# Revit family: Malvestio_Delta 4_CriticalCare___
name_source: partatom
category: Furniture
revit_build: Autodesk Revit 2018 (Build: 20190510_1515(x64)
units: mm (PartAtom-declared; Revit-internal decimal feet)

## family parameters
Always vertical = Yes
Cut with Voids When Loaded = No
OmniClass Number = 23.40.20.17.14.11
OmniClass Title = Beds
Room Calculation Point = No
Shared = No
Work Plane-Based = No

## types (2) — shared parameters
Bed_H Max = 800 mm
Bed_H Min = 390 mm
Bed_Inc Max = 16.00°
Bed_Inc Min = -16.00°
Bed_Lat Max = 15.00°
Bed_Lat Min = -15.00°
Blanket and Surpevisor Holder = Yes
DIM_Depth = 1000 mm  [stored 3.28084 ft]
DIM_Height = 1300 mm  [stored 4.26509 ft]
DIM_Mattress_Thick = 150 mm  [stored 0.492126 ft]
DIM_Width = 2200 mm
Ele_FL Amps = 0 A
Ele_Frequency = 50 Hz
Ele_Power = 0 W
Ele_Volts = 240 V
Frame_Base offset = 190 mm  [stored 0.62336 ft]
Frame_Boom = 540 mm
Frame_Top width = 255 mm  [stored 0.836614 ft]
Keynote = 0
Manufacturer = Malvestio Spa
Mat_Bump = Rubber Gray
Mat_CallUp = RAL 7032
Mat_Case = RAL 9010
Mat_Panel = RAL 9010
Mat_Panel_Logo = AB 425_Lilla Erica
Mat_Weel_Tyre = Rubber Black
Product Disclaimer = Malvestio Spa declines any responsibility for
the modifications of the type parameters.
The company is not responsible for the
objects/drawings and the correct
production/installation.
The company reserves the right to make technical
improvements or modifications of any type without
prior notice to the customer.
All rights reserved.
Product Series = Delta 4
Product URL = https://www.malvestio.com
URL = https://www.malvestio.com
Weighing System = Yes
Weight = 240.00 kg

## per-type parameters (varying)
| type | Electric Controls Side-Rails | Model | Product Code | Product Model |
| 3730B_AB 425_Lilla Erica | No | 3730B | 3730B | 3730B |
| 3750B_AB 425_Lilla Erica | Yes | 3750B | 3750B | 3750B |

note: [stored X ft] marks values corroborated as IEEE doubles in the binary element streams (Revit-internal decimal feet)

## geometry (parser evidence)
native form markers: Sweep x30
no freeform markers — native parametric forms only
